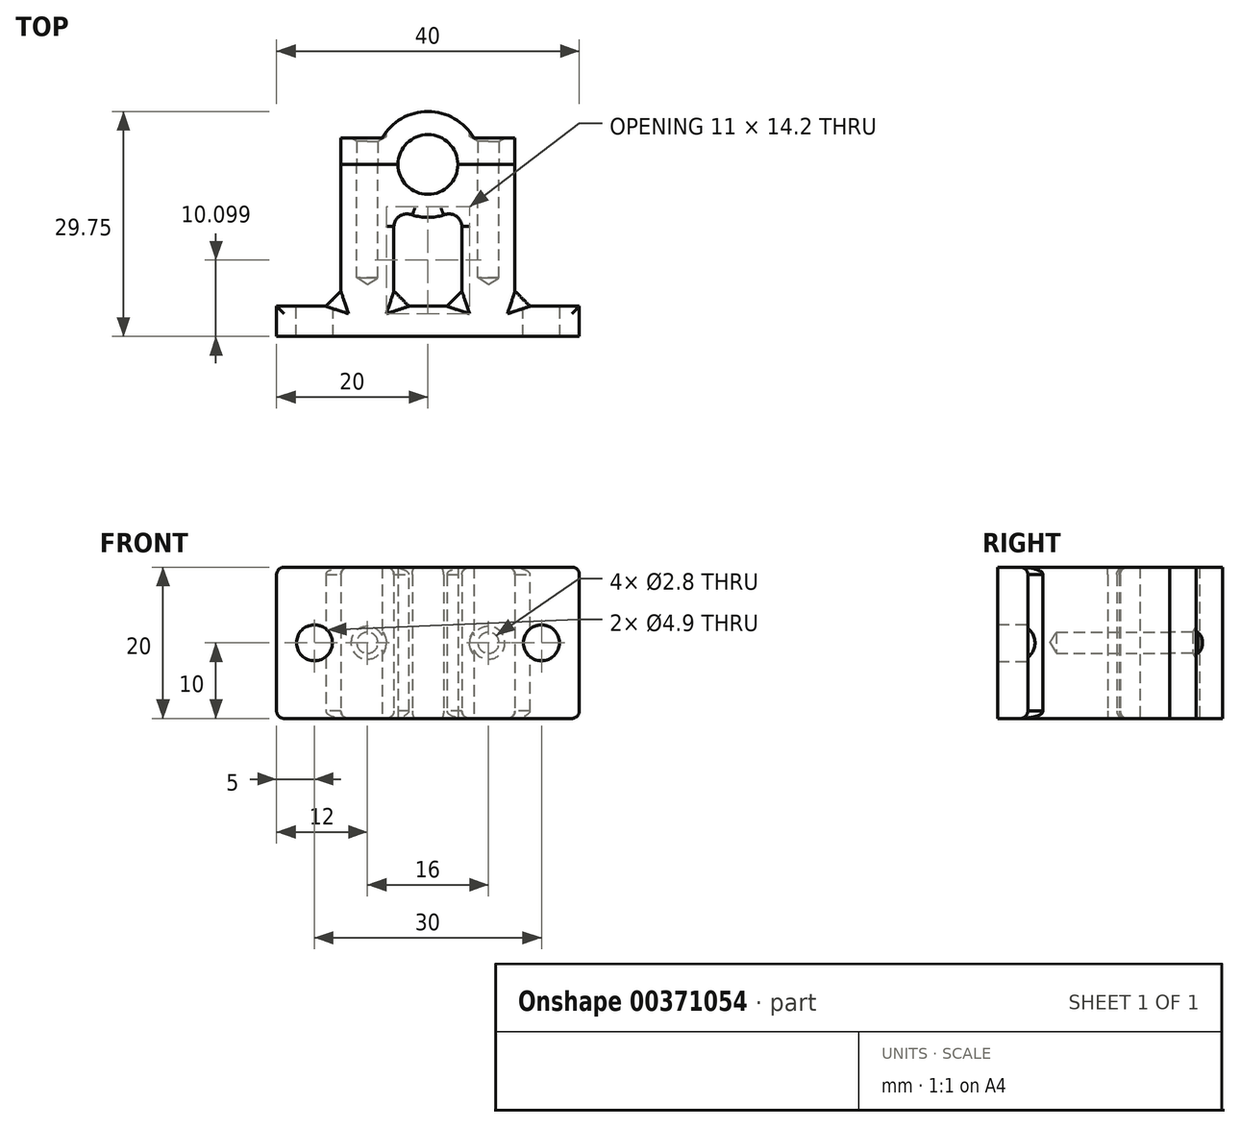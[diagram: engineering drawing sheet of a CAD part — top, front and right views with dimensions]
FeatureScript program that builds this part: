
annotation { "Feature Type Name" : "Feature", "Feature Type Description" : "" }
export const myFeature = defineFeature(function(context is Context, id is Id, definition is map)
    precondition{}
    {
        {
            var Q0;
            Q0=qCreatedBy(makeId("Top.planeOp"),FACE);
            var sketch = newSketch(context, id + "F0", { "sketchPlane" : qUnion([Q0])});
            skCircle(sketch, "E0", {"center": v(0, 0) * mm, "radius": 3.95 * mm, "construction": true});
            skLineSegment(sketch, "E1.bottom", {"start": v(-10, -22.75) * mm, "end": v(10, -22.75) * mm, "construction": true});
            skLineSegment(sketch, "E1.top", {"start": v(-10, 22.75) * mm, "end": v(10, 22.75) * mm, "construction": true});
            skLineSegment(sketch, "E1.left", {"start": v(-11.5, -22.75) * mm, "end": v(-11.5, 22.75) * mm, "construction": true});
            skLineSegment(sketch, "E1.right", {"start": v(11.5, -22.75) * mm, "end": v(11.5, 22.75) * mm, "construction": true});
            skLineSegment(sketch, "E2", {"start": v(0, 43.17) * mm, "end": v(0, -47.97) * mm, "construction": true});
            skPoint(sketch, "E2.startSnap0", {"position": v(0, -22.75) * mm});
            skLineSegment(sketch, "E3", {"start": v(-33.18, 0) * mm, "end": v(22.99, 0) * mm, "construction": true});
            skLineSegment(sketch, "E4", {"start": v(-3.95, 0) * mm, "end": v(-11.5, 0) * mm});
            skLineSegment(sketch, "E5", {"start": v(3.95, 0) * mm, "end": v(11.5, 0) * mm});
            skArc(sketch, "E6", {"start": v(-3.95, 0) * mm, "mid": v(0, 3.95) * mm, "end": v(3.95, 0) * mm});
            skArc(sketch, "E7", {"start": v(3.95, 0) * mm, "mid": v(0, -3.95) * mm, "end": v(-3.95, 0) * mm});
            skArc(sketch, "E8", {"start": v(7, 0) * mm, "mid": v(0, 7) * mm, "end": v(-7, 0) * mm, "construction": true});
            skLineSegment(sketch, "E9", {"start": v(-11.5, 0) * mm, "end": v(-11.5, 3.5) * mm});
            skLineSegment(sketch, "E10", {"start": v(-6.06, 3.5) * mm, "end": v(-11.5, 3.5) * mm});
            skLineSegment(sketch, "E11", {"start": v(6.06, 3.5) * mm, "end": v(11.5, 3.5) * mm});
            skLineSegment(sketch, "E12", {"start": v(11.5, 0) * mm, "end": v(11.5, 3.5) * mm});
            skArc(sketch, "E13", {"start": v(-6.06, 3.5) * mm, "mid": v(0, 7) * mm, "end": v(6.06, 3.5) * mm});
            skLineSegment(sketch, "E14.0", {"start": v(-9.14, -18.75) * mm, "end": v(10, -18.75) * mm, "construction": true});
            skLineSegment(sketch, "E15", {"start": v(-15, -18.75) * mm, "end": v(-9.14, -18.75) * mm});
            skLineSegment(sketch, "E16", {"start": v(-11.5, -18.75) * mm, "end": v(-11.5, 0) * mm});
            skLineSegment(sketch, "E17", {"start": v(15, -18.75) * mm, "end": v(10, -18.75) * mm});
            skLineSegment(sketch, "E18", {"start": v(11.5, -18.75) * mm, "end": v(11.5, 0) * mm});
            skArc(sketch, "E19", {"start": v(7, 0) * mm, "mid": v(0, -7) * mm, "end": v(-7, 0) * mm, "construction": true});
            skArc(sketch, "E20", {"start": v(-6, -3.6) * mm, "mid": v(0, -7) * mm, "end": v(6, -3.6) * mm});
            skPoint(sketch, "E21.endSnap0", {"position": v(-5.17, 3.5) * mm});
            skArc(sketch, "E22", {"start": v(-2.07, -6.69) * mm, "mid": v(-3.67, -6.8) * mm, "end": v(-4.5, -8.18) * mm});
            skArc(sketch, "E23.MirrorCS", {"start": v(2.07, -6.69) * mm, "mid": v(3.67, -6.8) * mm, "end": v(4.5, -8.18) * mm});
            skLineSegment(sketch, "E24", {"start": v(20, -22.75) * mm, "end": v(20, -18.75) * mm});
            skLineSegment(sketch, "E25", {"start": v(20, -18.75) * mm, "end": v(15, -18.75) * mm});
            skLineSegment(sketch, "E26.MirrorCS", {"start": v(-20, -18.75) * mm, "end": v(-15, -18.75) * mm});
            skLineSegment(sketch, "E27.MirrorCS", {"start": v(-20, -22.75) * mm, "end": v(-20, -18.75) * mm});
            skLineSegment(sketch, "E28.MirrorCS", {"start": v(-15, -26.7) * mm, "end": v(-15, 26.7) * mm, "construction": true});
            skLineSegment(sketch, "E29.MirrorCS", {"start": v(15, -26.7) * mm, "end": v(15, 26.7) * mm, "construction": true});
            skLineSegment(sketch, "E30", {"start": v(-20, -22.75) * mm, "end": v(20, -22.75) * mm});
            skLineSegment(sketch, "E31", {"start": v(4.5, -8.18) * mm, "end": v(4.5, -18.75) * mm});
            skLineSegment(sketch, "E32", {"start": v(4.5, -18.75) * mm, "end": v(-4.5, -18.75) * mm});
            skLineSegment(sketch, "E33.MirrorCS", {"start": v(-4.5, -8.18) * mm, "end": v(-4.5, -18.75) * mm});
            skSolve(sketch);
        }
        {
            var Q0;
            Q0=qCreatedBy(makeId("Front.planeOp"),FACE);
            var sketch = newSketch(context, id + "F1", { "sketchPlane" : qUnion([Q0])});
            skLineSegment(sketch, "E34", {"start": v(0, 0) * mm, "end": v(0, 20) * mm, "construction": true});
            skLineSegment(sketch, "E35", {"start": v(0, 20) * mm, "end": v(20, 20) * mm, "construction": true});
            skLineSegment(sketch, "E36", {"start": v(20, 20) * mm, "end": v(20, 0) * mm, "construction": true});
            skLineSegment(sketch, "E37", {"start": v(20, 0) * mm, "end": v(0, 0) * mm, "construction": true});
            skLineSegment(sketch, "E38.MirrorCS", {"start": v(0, 20) * mm, "end": v(-20, 20) * mm, "construction": true});
            skLineSegment(sketch, "E39.MirrorCS", {"start": v(-20, 0) * mm, "end": v(0, 0) * mm, "construction": true});
            skLineSegment(sketch, "E40.MirrorCS", {"start": v(-20, 20) * mm, "end": v(-20, 0) * mm, "construction": true});
            skLineSegment(sketch, "E41.MirrorCS", {"start": v(6, 20) * mm, "end": v(6, 0) * mm, "construction": true});
            skLineSegment(sketch, "E42.MirrorCS", {"start": v(10, 20) * mm, "end": v(10, 0) * mm, "construction": true});
            skLineSegment(sketch, "E43", {"start": v(-20, 20) * mm, "end": v(-10, 0) * mm, "construction": true});
            skLineSegment(sketch, "E44", {"start": v(-10, 20) * mm, "end": v(-20, 0) * mm, "construction": true});
            skLineSegment(sketch, "E45.MirrorCS", {"start": v(10, 20) * mm, "end": v(6, 0) * mm, "construction": true});
            skLineSegment(sketch, "E46.MirrorCS", {"start": v(6, 20) * mm, "end": v(10, 0) * mm, "construction": true});
            skLineSegment(sketch, "E47.MirrorCS", {"start": v(20, 20) * mm, "end": v(10, 0) * mm, "construction": true});
            skLineSegment(sketch, "E48.MirrorCS", {"start": v(10, 20) * mm, "end": v(20, 0) * mm, "construction": true});
            skLineSegment(sketch, "E49.MirrorCS", {"start": v(15, 10) * mm, "end": v(8, 10) * mm, "construction": true});
            skLineSegment(sketch, "E50.MirrorCS", {"start": v(-10, 20) * mm, "end": v(-10, 0) * mm, "construction": true});
            skLineSegment(sketch, "E51.MirrorCS", {"start": v(-10, 20) * mm, "end": v(-6, 0) * mm, "construction": true});
            skLineSegment(sketch, "E52.MirrorCS", {"start": v(-6, 20) * mm, "end": v(-10, 0) * mm, "construction": true});
            skLineSegment(sketch, "E53.MirrorCS", {"start": v(-6, 20) * mm, "end": v(-6, 0) * mm, "construction": true});
            skLineSegment(sketch, "E54.MirrorCS", {"start": v(-15, 10) * mm, "end": v(-8, 10) * mm, "construction": true});
            skSolve(sketch);
        }
        {
            var Q0;
            Q0=makeQuery(id+"F0.imprint","IMPRINT",FACE,{"disambiguationData":[TD([[makeQuery(id+"F0.imprint","IMPRINT",EDGE,{"derivedFrom":sQuery(id+"F0.wireOp",EDGE,"E4")}),1.0]])]});
            var Q1;
            {var subQ0=sQuery(id+"F0.wireOp",EDGE,"E20");var subQ1=sQuery(id+"F0.wireOp",EDGE,"fGXx5mKk-028a-ssRt-KOYL-Ndiq90U5VOPl");var subQ2=makeQuery(id+"F0.imprint","INTERSECT",VERTEX,{"derivedFrom":[subQ1,subQ0]});Q1=makeQuery(id+"F0.imprint","IMPRINT",FACE,{"disambiguationData":[TD([[makeQuery(id+"F0.imprint","IMPRINT",EDGE,{"disambiguationData":[TD([[subQ2,-1.0]])],"derivedFrom":subQ1}),1.0]])]});}
            var Q2;
            {var subQ0=sQuery(id+"F0.wireOp",EDGE,"E20");var subQ1=sQuery(id+"F0.wireOp",EDGE,"CvSH9Qos-IBVu-BQQu-liTP-uIPj88FDEuSd");var subQ2=makeQuery(id+"F0.imprint","INTERSECT",VERTEX,{"derivedFrom":[subQ1,subQ0]});Q2=makeQuery(id+"F0.imprint","IMPRINT",FACE,{"disambiguationData":[TD([[makeQuery(id+"F0.imprint","IMPRINT",EDGE,{"disambiguationData":[TD([[subQ2,1.0]])],"derivedFrom":subQ1}),1.0]])]});}
            var Q3;
            {var subQ0=sQuery(id+"F0.wireOp",EDGE,"E17");Q3=makeQuery(id+"F0.imprint","IMPRINT",FACE,{"disambiguationData":[TD([[makeQuery(id+"F0.imprint","IMPRINT",EDGE,{"derivedFrom":subQ0}),-1.0]])]});}
            var Q4;
            {var subQ3=sQuery(id+"F0.wireOp",EDGE,"ceada07a-6df1-444d-bf8f-508dd2f25667");Q4=makeQuery(id+"F0.imprint","IMPRINT",FACE,{"disambiguationData":[TD([[makeQuery(id+"F0.imprint","IMPRINT",EDGE,{"derivedFrom":subQ3}),-1.0]])]});}
            var Q5;
            {var subQ3=sQuery(id+"F0.wireOp",EDGE,"21435801-f3ad-4afe-81ca-bc311d5c01770.MirrorCS");Q5=makeQuery(id+"F0.imprint","IMPRINT",FACE,{"disambiguationData":[TD([[makeQuery(id+"F0.imprint","IMPRINT",EDGE,{"derivedFrom":subQ3}),1.0]])]});}
            var Q6;
            {var subQ0=sQuery(id+"F0.wireOp",EDGE,"E15");Q6=makeQuery(id+"F0.imprint","IMPRINT",FACE,{"disambiguationData":[TD([[makeQuery(id+"F0.imprint","IMPRINT",EDGE,{"derivedFrom":subQ0}),1.0]])]});}
            var Q7;
            {var subQ0=sQuery(id+"F0.wireOp",EDGE,"fiYNvXtu-JcpG-wVFz-9FR0-CaiYWWEELGmy");Q7=makeQuery(id+"F0.imprint","IMPRINT",FACE,{"disambiguationData":[TD([[makeQuery(id+"F0.imprint","IMPRINT",EDGE,{"derivedFrom":subQ0}),1.0]])]});}
            var Q8;
            {var subQ2=sQuery(id+"F0.wireOp",EDGE,"E26.MirrorCS");Q8=makeQuery(id+"F0.imprint","IMPRINT",FACE,{"disambiguationData":[TD([[makeQuery(id+"F0.imprint","IMPRINT",EDGE,{"derivedFrom":subQ2}),-1.0]])]});}
            extrude(context, id + "F2", {"entities" : qUnion([Q0, Q1, Q2, Q3, Q4, Q5, Q6, Q7, Q8]), "depth" : 20 * mm});
        }
        {
            var Q0;
            Q0=makeQuery(id+"F0.imprint","IMPRINT",FACE,{"disambiguationData":[TD([[makeQuery(id+"F0.imprint","IMPRINT",EDGE,{"derivedFrom":sQuery(id+"F0.wireOp",EDGE,"E4")}),-1.0]])]});
            var Q1;
            {var subQ0=sQuery(id+"F0.wireOp",EDGE,"E10");Q1=makeQuery(id+"F0.imprint","IMPRINT",FACE,{"disambiguationData":[TD([[makeQuery(id+"F0.imprint","IMPRINT",EDGE,{"derivedFrom":subQ0}),-1.0]])]});}
            var Q2;
            {var subQ0=sQuery(id+"F0.wireOp",EDGE,"E11");Q2=makeQuery(id+"F0.imprint","IMPRINT",FACE,{"disambiguationData":[TD([[makeQuery(id+"F0.imprint","IMPRINT",EDGE,{"derivedFrom":subQ0}),1.0]])]});}
            extrude(context, id + "F3", {"entities" : qUnion([Q0, Q1, Q2]), "depth" : 20 * mm});
        }
        {
            var Q0;
            Q0=sQuery(id+"F1.wireOp",VERTEX,"zXXnKSf7-GhJt-SI1w-yzcV-klMIAKRFoqqE.start");
            var Q1;
            Q1=sQuery(id+"F1.wireOp",VERTEX,"E49.MirrorCS.start");
            var Q2;
            Q2=makeQuery(id+"F2.opExtrude","SWEPT_BODY",BODY,{"disambiguationData":[OSD([sQuery(id+"F0.wireOp",EDGE,"E4"),sQuery(id+"F0.wireOp",EDGE,"E5"),sQuery(id+"F0.wireOp",EDGE,"E7"),sQuery(id+"F0.wireOp",EDGE,"Qp0b4A5F-PEZz-WxIl-w85g-mMOqEHtGHs0Y"),sQuery(id+"F0.wireOp",EDGE,"3GZM9fG6-5eXR-hhPL-hdbV-YrBfE3BmG3J5"),sQuery(id+"F0.wireOp",EDGE,"E16"),sQuery(id+"F0.wireOp",EDGE,"YOUf0rZS-7agO-fim9-izvp-ucZtZaTmQyXM"),sQuery(id+"F0.wireOp",EDGE,"E18"),sQuery(id+"F0.wireOp",EDGE,"fGXx5mKk-028a-ssRt-KOYL-Ndiq90U5VOPl"),sQuery(id+"F0.wireOp",EDGE,"KvWkPdP2-N5Ae-fyOq-ppFJ-d0FditwGePsY"),sQuery(id+"F0.wireOp",EDGE,"CvSH9Qos-IBVu-BQQu-liTP-uIPj88FDEuSd"),sQuery(id+"F0.wireOp",EDGE,"E20"),sQuery(id+"F0.wireOp",EDGE,"E22"),sQuery(id+"F0.wireOp",EDGE,"E23.MirrorCS"),sQuery(id+"F0.wireOp",EDGE,"lmKCdi61-SYqH-588H-mFMN-USzl79AIN7qr"),sQuery(id+"F0.wireOp",EDGE,"2fa183ca-1ded-41c0-80e5-ca687e3a55230.MirrorCS"),sQuery(id+"F0.wireOp",EDGE,"ceada07a-6df1-444d-bf8f-508dd2f25667"),sQuery(id+"F0.wireOp",EDGE,"21435801-f3ad-4afe-81ca-bc311d5c01770.MirrorCS")])]});
            hole(context, id + "F4", {"style" : HoleStyle.SIMPLE, "endStyle" : HoleEndStyle.BLIND, "oppositeDirection" : true, "holeDiameter" : 2.5 * mm, "holeDepth" : 30 * mm, "isTappedThrough" : true, "tappedDepth" : 12 * mm, "tapClearance" : 3, "locations" : qUnion([Q0, Q1]), "scope" : qUnion([Q2])});
        }
        {
            var Q0;
            Q0=sQuery(id+"F1.wireOp",VERTEX,"zXXnKSf7-GhJt-SI1w-yzcV-klMIAKRFoqqE.end");
            var Q1;
            Q1=sQuery(id+"F1.wireOp",VERTEX,"E49.MirrorCS.end");
            var Q2;
            Q2=sQuery(id+"F1.wireOp",VERTEX,"E54.MirrorCS.end");
            var Q3;
            Q3=makeQuery(id+"F3.opExtrude","SWEPT_BODY",BODY,{"disambiguationData":[OSD([sQuery(id+"F0.wireOp",EDGE,"E4"),sQuery(id+"F0.wireOp",EDGE,"E5"),sQuery(id+"F0.wireOp",EDGE,"E6"),sQuery(id+"F0.wireOp",EDGE,"E9"),sQuery(id+"F0.wireOp",EDGE,"E12"),sQuery(id+"F0.wireOp",EDGE,"E13"),sQuery(id+"F0.wireOp",EDGE,"E21"),sQuery(id+"F0.wireOp",EDGE,"c25b683a-cc0d-4ae4-92c7-48c638fb54a90.MirrorCS")])]});
            hole(context, id + "F5", {"style" : HoleStyle.SIMPLE, "endStyle" : HoleEndStyle.BLIND, "holeDiameter" : 2.8 * mm, "holeDepth" : 10 * mm, "isTappedThrough" : true, "tappedDepth" : 12 * mm, "tapClearance" : 3, "locations" : qUnion([Q0, Q1, Q2]), "scope" : qUnion([Q3])});
        }
        {
            var Q0;
            Q0=sQuery(id+"F1.wireOp",VERTEX,"zXXnKSf7-GhJt-SI1w-yzcV-klMIAKRFoqqE.end");
            var Q1;
            Q1=sQuery(id+"F1.wireOp",VERTEX,"E49.MirrorCS.end");
            var Q2;
            Q2=sQuery(id+"F1.wireOp",VERTEX,"E54.MirrorCS.end");
            var Q3;
            Q3=makeQuery(id+"F2.opExtrude","SWEPT_BODY",BODY,{"disambiguationData":[OSD([sQuery(id+"F0.wireOp",EDGE,"E4"),sQuery(id+"F0.wireOp",EDGE,"E5"),sQuery(id+"F0.wireOp",EDGE,"E7"),sQuery(id+"F0.wireOp",EDGE,"Qp0b4A5F-PEZz-WxIl-w85g-mMOqEHtGHs0Y"),sQuery(id+"F0.wireOp",EDGE,"3GZM9fG6-5eXR-hhPL-hdbV-YrBfE3BmG3J5"),sQuery(id+"F0.wireOp",EDGE,"E16"),sQuery(id+"F0.wireOp",EDGE,"YOUf0rZS-7agO-fim9-izvp-ucZtZaTmQyXM"),sQuery(id+"F0.wireOp",EDGE,"E18"),sQuery(id+"F0.wireOp",EDGE,"fGXx5mKk-028a-ssRt-KOYL-Ndiq90U5VOPl"),sQuery(id+"F0.wireOp",EDGE,"KvWkPdP2-N5Ae-fyOq-ppFJ-d0FditwGePsY"),sQuery(id+"F0.wireOp",EDGE,"CvSH9Qos-IBVu-BQQu-liTP-uIPj88FDEuSd"),sQuery(id+"F0.wireOp",EDGE,"E20"),sQuery(id+"F0.wireOp",EDGE,"E22"),sQuery(id+"F0.wireOp",EDGE,"E23.MirrorCS"),sQuery(id+"F0.wireOp",EDGE,"lmKCdi61-SYqH-588H-mFMN-USzl79AIN7qr"),sQuery(id+"F0.wireOp",EDGE,"2fa183ca-1ded-41c0-80e5-ca687e3a55230.MirrorCS"),sQuery(id+"F0.wireOp",EDGE,"ceada07a-6df1-444d-bf8f-508dd2f25667"),sQuery(id+"F0.wireOp",EDGE,"21435801-f3ad-4afe-81ca-bc311d5c01770.MirrorCS")])]});
            hole(context, id + "F6", {"style" : HoleStyle.SIMPLE, "endStyle" : HoleEndStyle.BLIND, "oppositeDirection" : true, "holeDiameter" : 2.8 * mm, "holeDepth" : 15 * mm, "isTappedThrough" : true, "tappedDepth" : 12 * mm, "tapClearance" : 3, "locations" : qUnion([Q0, Q1, Q2]), "scope" : qUnion([Q3])});
        }
        {
            var Q0;
            Q0=sQuery(id+"F1.wireOp",VERTEX,"zXXnKSf7-GhJt-SI1w-yzcV-klMIAKRFoqqE.start");
            var Q1;
            Q1=sQuery(id+"F1.wireOp",VERTEX,"E49.MirrorCS.start");
            var Q2;
            Q2=sQuery(id+"F1.wireOp",VERTEX,"E54.MirrorCS.start");
            var Q3;
            Q3=makeQuery(id+"F2.opExtrude","SWEPT_BODY",BODY,{"disambiguationData":[OSD([sQuery(id+"F0.wireOp",EDGE,"E4"),sQuery(id+"F0.wireOp",EDGE,"E5"),sQuery(id+"F0.wireOp",EDGE,"E7"),sQuery(id+"F0.wireOp",EDGE,"Qp0b4A5F-PEZz-WxIl-w85g-mMOqEHtGHs0Y"),sQuery(id+"F0.wireOp",EDGE,"3GZM9fG6-5eXR-hhPL-hdbV-YrBfE3BmG3J5"),sQuery(id+"F0.wireOp",EDGE,"E16"),sQuery(id+"F0.wireOp",EDGE,"YOUf0rZS-7agO-fim9-izvp-ucZtZaTmQyXM"),sQuery(id+"F0.wireOp",EDGE,"E18"),sQuery(id+"F0.wireOp",EDGE,"fGXx5mKk-028a-ssRt-KOYL-Ndiq90U5VOPl"),sQuery(id+"F0.wireOp",EDGE,"KvWkPdP2-N5Ae-fyOq-ppFJ-d0FditwGePsY"),sQuery(id+"F0.wireOp",EDGE,"CvSH9Qos-IBVu-BQQu-liTP-uIPj88FDEuSd"),sQuery(id+"F0.wireOp",EDGE,"E20"),sQuery(id+"F0.wireOp",EDGE,"E22"),sQuery(id+"F0.wireOp",EDGE,"E23.MirrorCS"),sQuery(id+"F0.wireOp",EDGE,"lmKCdi61-SYqH-588H-mFMN-USzl79AIN7qr"),sQuery(id+"F0.wireOp",EDGE,"2fa183ca-1ded-41c0-80e5-ca687e3a55230.MirrorCS"),sQuery(id+"F0.wireOp",EDGE,"ceada07a-6df1-444d-bf8f-508dd2f25667"),sQuery(id+"F0.wireOp",EDGE,"21435801-f3ad-4afe-81ca-bc311d5c01770.MirrorCS")])]});
            hole(context, id + "F7", {"style" : HoleStyle.SIMPLE, "endStyle" : HoleEndStyle.BLIND, "oppositeDirection" : true, "holeDiameter" : 4.9 * mm, "holeDepth" : 22.7 * mm, "isTappedThrough" : true, "tappedDepth" : 12 * mm, "tapClearance" : 3, "startFromSketch" : true, "locations" : qUnion([Q0, Q1, Q2]), "scope" : qUnion([Q3])});
        }
        {
            var Q0;
            Q0=qCreatedBy(makeId("Front.planeOp"),FACE);
            cPlane(context, id + "F8", {"entities" : qUnion([Q0]), "cplaneType" : CPlaneType.OFFSET, "offset" : 7 * mm, "oppositeDirection" : true, "width" : 150 * mm, "height" : 150 * mm});
        }
        {
            var Q0;
            Q0=qCreatedBy(id+"F8.planeOp",FACE);
            var sketch = newSketch(context, id + "F9", { "sketchPlane" : qUnion([Q0])});
            skLineSegment(sketch, "E55", {"start": v(0, 0) * mm, "end": v(0, 20) * mm, "construction": true});
            skLineSegment(sketch, "E56", {"start": v(0, 20) * mm, "end": v(15, 20) * mm, "construction": true});
            skLineSegment(sketch, "E57", {"start": v(15, 20) * mm, "end": v(15, 0) * mm, "construction": true});
            skLineSegment(sketch, "E58", {"start": v(15, 0) * mm, "end": v(0, 0) * mm, "construction": true});
            skLineSegment(sketch, "E59.MirrorCS", {"start": v(0, 20) * mm, "end": v(-15, 20) * mm, "construction": true});
            skLineSegment(sketch, "E60.MirrorCS", {"start": v(-15, 0) * mm, "end": v(0, 0) * mm, "construction": true});
            skLineSegment(sketch, "E61.MirrorCS", {"start": v(-15, 20) * mm, "end": v(-15, 0) * mm, "construction": true});
            skLineSegment(sketch, "E62.0", {"start": v(-10, 20) * mm, "end": v(-10, 0) * mm, "construction": true});
            skLineSegment(sketch, "E63.0", {"start": v(-6, 20) * mm, "end": v(-6, 0) * mm, "construction": true});
            skLineSegment(sketch, "E64.MirrorCS", {"start": v(6, 20) * mm, "end": v(6, 0) * mm, "construction": true});
            skLineSegment(sketch, "E65.MirrorCS", {"start": v(10, 20) * mm, "end": v(10, 0) * mm, "construction": true});
            skLineSegment(sketch, "E66", {"start": v(-15, 20) * mm, "end": v(-10, 0) * mm, "construction": true});
            skLineSegment(sketch, "E67", {"start": v(-10, 10) * mm, "end": v(-15, 0) * mm, "construction": true});
            skLineSegment(sketch, "E68", {"start": v(-10, 20) * mm, "end": v(-6, 0) * mm, "construction": true});
            skLineSegment(sketch, "E69", {"start": v(-6, 20) * mm, "end": v(-10, 0) * mm, "construction": true});
            skLineSegment(sketch, "E70.MirrorCS", {"start": v(10, 20) * mm, "end": v(6, 0) * mm, "construction": true});
            skLineSegment(sketch, "E71.MirrorCS", {"start": v(6, 20) * mm, "end": v(10, 0) * mm, "construction": true});
            skLineSegment(sketch, "E72.MirrorCS", {"start": v(15, 20) * mm, "end": v(10, 0) * mm, "construction": true});
            skLineSegment(sketch, "E73.MirrorCS", {"start": v(10, 10) * mm, "end": v(15, 0) * mm, "construction": true});
            skLineSegment(sketch, "E74", {"start": v(-12.5, 10) * mm, "end": v(-8, 10) * mm, "construction": true});
            skLineSegment(sketch, "E75.MirrorCS", {"start": v(12.5, 10) * mm, "end": v(8, 10) * mm, "construction": true});
            skSolve(sketch);
        }
        {
            var Q0;
            Q0=sQuery(id+"F9.wireOp",VERTEX,"E75.MirrorCS.end");
            var Q1;
            Q1=sQuery(id+"F9.wireOp",VERTEX,"E74.end");
            var Q2;
            Q2=makeQuery(id+"F3.opExtrude","SWEPT_BODY",BODY,{"disambiguationData":[OSD([sQuery(id+"F0.wireOp",EDGE,"E4"),sQuery(id+"F0.wireOp",EDGE,"E5"),sQuery(id+"F0.wireOp",EDGE,"E6"),sQuery(id+"F0.wireOp",EDGE,"E9"),sQuery(id+"F0.wireOp",EDGE,"E12"),sQuery(id+"F0.wireOp",EDGE,"E13"),sQuery(id+"F0.wireOp",EDGE,"E21"),sQuery(id+"F0.wireOp",EDGE,"c25b683a-cc0d-4ae4-92c7-48c638fb54a90.MirrorCS")])]});
            hole(context, id + "F10", {"style" : HoleStyle.SIMPLE, "endStyle" : HoleEndStyle.BLIND, "oppositeDirection" : true, "holeDiameter" : 5 * mm, "holeDepth" : 3.3 * mm, "isTappedThrough" : true, "tappedDepth" : 12 * mm, "tapClearance" : 3, "startFromSketch" : true, "locations" : qUnion([Q0, Q1]), "scope" : qUnion([Q2])});
        }
        {
            var Q0;
            Q0=makeQuery(id+"F3.opExtrude","CAP_EDGE",EDGE,{"disambiguationData":[OSD([sQuery(id+"F0.wireOp",EDGE,"E12")])],"isStart":true});
            var Q1;
            Q1=makeQuery(id+"F2.opExtrude","CAP_EDGE",EDGE,{"disambiguationData":[OSD([sQuery(id+"F0.wireOp",EDGE,"E18")])],"isStart":true});
            var Q2;
            Q2=makeQuery(id+"F2.opExtrude","CAP_EDGE",EDGE,{"disambiguationData":[OSD([sQuery(id+"F0.wireOp",EDGE,"2fa183ca-1ded-41c0-80e5-ca687e3a55230.MirrorCS")])],"isStart":true});
            var Q3;
            Q3=makeQuery(id+"F2.opExtrude","CAP_EDGE",EDGE,{"disambiguationData":[OSD([sQuery(id+"F0.wireOp",EDGE,"lmKCdi61-SYqH-588H-mFMN-USzl79AIN7qr")])],"isStart":true});
            var Q4;
            Q4=makeQuery(id+"F2.opExtrude","CAP_EDGE",EDGE,{"disambiguationData":[OSD([sQuery(id+"F0.wireOp",EDGE,"E16")])],"isStart":true});
            var Q5;
            Q5=makeQuery(id+"F3.opExtrude","CAP_EDGE",EDGE,{"disambiguationData":[OSD([sQuery(id+"F0.wireOp",EDGE,"E9")])],"isStart":true});
            var Q6;
            Q6=makeQuery(id+"F2.opExtrude","CAP_EDGE",EDGE,{"disambiguationData":[OSD([sQuery(id+"F0.wireOp",EDGE,"lmKCdi61-SYqH-588H-mFMN-USzl79AIN7qr")])],"isStart":false});
            var Q7;
            Q7=makeQuery(id+"F2.opExtrude","CAP_EDGE",EDGE,{"disambiguationData":[OSD([sQuery(id+"F0.wireOp",EDGE,"E16")])],"isStart":false});
            var Q8;
            Q8=makeQuery(id+"F3.opExtrude","CAP_EDGE",EDGE,{"disambiguationData":[OSD([sQuery(id+"F0.wireOp",EDGE,"E9")])],"isStart":false});
            var Q9;
            Q9=makeQuery(id+"F2.opExtrude","CAP_EDGE",EDGE,{"disambiguationData":[OSD([sQuery(id+"F0.wireOp",EDGE,"2fa183ca-1ded-41c0-80e5-ca687e3a55230.MirrorCS")])],"isStart":false});
            var Q10;
            Q10=makeQuery(id+"F2.opExtrude","CAP_EDGE",EDGE,{"disambiguationData":[OSD([sQuery(id+"F0.wireOp",EDGE,"E18")])],"isStart":false});
            var Q11;
            Q11=makeQuery(id+"F3.opExtrude","CAP_EDGE",EDGE,{"disambiguationData":[OSD([sQuery(id+"F0.wireOp",EDGE,"E12")])],"isStart":false});
            var Q12;
            Q12=makeQuery(id+"F2.opExtrude","CAP_EDGE",EDGE,{"disambiguationData":[OSD([sQuery(id+"F0.wireOp",EDGE,"ceada07a-6df1-444d-bf8f-508dd2f25667")])],"isStart":false});
            var Q13;
            Q13=makeQuery(id+"F2.opExtrude","CAP_EDGE",EDGE,{"disambiguationData":[OSD([sQuery(id+"F0.wireOp",EDGE,"21435801-f3ad-4afe-81ca-bc311d5c01770.MirrorCS")])],"isStart":false});
            var Q14;
            Q14=makeQuery(id+"F2.opExtrude","CAP_EDGE",EDGE,{"disambiguationData":[OSD([sQuery(id+"F0.wireOp",EDGE,"fGXx5mKk-028a-ssRt-KOYL-Ndiq90U5VOPl")])],"isStart":false});
            var Q15;
            Q15=makeQuery(id+"F2.opExtrude","CAP_EDGE",EDGE,{"disambiguationData":[OSD([sQuery(id+"F0.wireOp",EDGE,"E22")])],"isStart":false});
            var Q16;
            Q16=makeQuery(id+"F2.opExtrude","CAP_EDGE",EDGE,{"disambiguationData":[OSD([sQuery(id+"F0.wireOp",EDGE,"E20")])],"isStart":false});
            var Q17;
            Q17=makeQuery(id+"F2.opExtrude","CAP_EDGE",EDGE,{"disambiguationData":[OSD([sQuery(id+"F0.wireOp",EDGE,"E23.MirrorCS")])],"isStart":false});
            var Q18;
            Q18=makeQuery(id+"F2.opExtrude","CAP_EDGE",EDGE,{"disambiguationData":[OSD([sQuery(id+"F0.wireOp",EDGE,"CvSH9Qos-IBVu-BQQu-liTP-uIPj88FDEuSd")])],"isStart":false});
            var Q19;
            Q19=makeQuery(id+"F2.opExtrude","CAP_EDGE",EDGE,{"disambiguationData":[OSD([sQuery(id+"F0.wireOp",EDGE,"KvWkPdP2-N5Ae-fyOq-ppFJ-d0FditwGePsY")])],"isStart":false});
            var Q20;
            Q20=makeQuery(id+"F2.opExtrude","CAP_EDGE",EDGE,{"disambiguationData":[OSD([sQuery(id+"F0.wireOp",EDGE,"E22")])],"isStart":true});
            var Q21;
            Q21=makeQuery(id+"F2.opExtrude","CAP_EDGE",EDGE,{"disambiguationData":[OSD([sQuery(id+"F0.wireOp",EDGE,"E20")])],"isStart":true});
            var Q22;
            Q22=makeQuery(id+"F2.opExtrude","CAP_EDGE",EDGE,{"disambiguationData":[OSD([sQuery(id+"F0.wireOp",EDGE,"E23.MirrorCS")])],"isStart":true});
            var Q23;
            Q23=makeQuery(id+"F2.opExtrude","CAP_EDGE",EDGE,{"disambiguationData":[OSD([sQuery(id+"F0.wireOp",EDGE,"CvSH9Qos-IBVu-BQQu-liTP-uIPj88FDEuSd")])],"isStart":true});
            var Q24;
            Q24=makeQuery(id+"F2.opExtrude","CAP_EDGE",EDGE,{"disambiguationData":[OSD([sQuery(id+"F0.wireOp",EDGE,"ceada07a-6df1-444d-bf8f-508dd2f25667")])],"isStart":true});
            var Q25;
            Q25=makeQuery(id+"F2.opExtrude","CAP_EDGE",EDGE,{"disambiguationData":[OSD([sQuery(id+"F0.wireOp",EDGE,"KvWkPdP2-N5Ae-fyOq-ppFJ-d0FditwGePsY")])],"isStart":true});
            var Q26;
            Q26=makeQuery(id+"F2.opExtrude","CAP_EDGE",EDGE,{"disambiguationData":[OSD([sQuery(id+"F0.wireOp",EDGE,"21435801-f3ad-4afe-81ca-bc311d5c01770.MirrorCS")])],"isStart":true});
            var Q27;
            Q27=makeQuery(id+"F2.opExtrude","CAP_EDGE",EDGE,{"disambiguationData":[OSD([sQuery(id+"F0.wireOp",EDGE,"fGXx5mKk-028a-ssRt-KOYL-Ndiq90U5VOPl")])],"isStart":true});
            var Q28;
            Q28=makeQuery(id+"F2.opExtrude","CAP_EDGE",EDGE,{"disambiguationData":[OSD([sQuery(id+"F0.wireOp",EDGE,"3GZM9fG6-5eXR-hhPL-hdbV-YrBfE3BmG3J5")])],"isStart":true});
            var Q29;
            Q29=makeQuery(id+"F2.opExtrude","CAP_EDGE",EDGE,{"disambiguationData":[OSD([sQuery(id+"F0.wireOp",EDGE,"3GZM9fG6-5eXR-hhPL-hdbV-YrBfE3BmG3J5")])],"isStart":false});
            var Q30;
            Q30=makeQuery(id+"F2.opExtrude","CAP_EDGE",EDGE,{"disambiguationData":[OSD([sQuery(id+"F0.wireOp",EDGE,"YOUf0rZS-7agO-fim9-izvp-ucZtZaTmQyXM")])],"isStart":false});
            var Q31;
            Q31=makeQuery(id+"F2.opExtrude","CAP_EDGE",EDGE,{"disambiguationData":[OSD([sQuery(id+"F0.wireOp",EDGE,"YOUf0rZS-7agO-fim9-izvp-ucZtZaTmQyXM")])],"isStart":true});
            var Q32;
            Q32=makeQuery(id+"F2.opExtrude","CAP_EDGE",EDGE,{"disambiguationData":[OSD([sQuery(id+"F0.wireOp",EDGE,"E26.MirrorCS")])],"isStart":false});
            var Q33;
            Q33=makeQuery(id+"F2.opExtrude","CAP_EDGE",EDGE,{"disambiguationData":[OSD([sQuery(id+"F0.wireOp",EDGE,"E27.MirrorCS")])],"isStart":false});
            var Q34;
            Q34=makeQuery(id+"F2.opExtrude","CAP_EDGE",EDGE,{"disambiguationData":[OSD([sQuery(id+"F0.wireOp",EDGE,"E24")])],"isStart":false});
            var Q35;
            Q35=makeQuery(id+"F2.opExtrude","CAP_EDGE",EDGE,{"disambiguationData":[OSD([sQuery(id+"F0.wireOp",EDGE,"E25")])],"isStart":false});
            var Q36;
            Q36=makeQuery(id+"F2.opExtrude","CAP_EDGE",EDGE,{"disambiguationData":[OSD([sQuery(id+"F0.wireOp",EDGE,"E26.MirrorCS")])],"isStart":true});
            var Q37;
            Q37=makeQuery(id+"F2.opExtrude","CAP_EDGE",EDGE,{"disambiguationData":[OSD([sQuery(id+"F0.wireOp",EDGE,"E27.MirrorCS")])],"isStart":true});
            var Q38;
            Q38=makeQuery(id+"F2.opExtrude","CAP_EDGE",EDGE,{"disambiguationData":[OSD([sQuery(id+"F0.wireOp",EDGE,"E25")])],"isStart":true});
            var Q39;
            Q39=makeQuery(id+"F2.opExtrude","CAP_EDGE",EDGE,{"disambiguationData":[OSD([sQuery(id+"F0.wireOp",EDGE,"E24")])],"isStart":true});
            var Q40;
            Q40=makeQuery(id+"F2.opExtrude","CAP_EDGE",EDGE,{"disambiguationData":[OSD([sQuery(id+"F0.wireOp",EDGE,"E33.MirrorCS")])],"isStart":false});
            var Q41;
            Q41=makeQuery(id+"F2.opExtrude","CAP_EDGE",EDGE,{"disambiguationData":[OSD([sQuery(id+"F0.wireOp",EDGE,"E31")])],"isStart":false});
            var Q42;
            Q42=makeQuery(id+"F2.opExtrude","CAP_EDGE",EDGE,{"disambiguationData":[OSD([sQuery(id+"F0.wireOp",EDGE,"E33.MirrorCS")])],"isStart":true});
            var Q43;
            Q43=makeQuery(id+"F2.opExtrude","CAP_EDGE",EDGE,{"disambiguationData":[OSD([sQuery(id+"F0.wireOp",EDGE,"E31")])],"isStart":true});
            var Q44;
            Q44=makeQuery(id+"F2.opExtrude","CAP_EDGE",EDGE,{"disambiguationData":[OSD([sQuery(id+"F0.wireOp",EDGE,"E32")])],"isStart":true});
            var Q45;
            Q45=makeQuery(id+"F2.opExtrude","CAP_EDGE",EDGE,{"disambiguationData":[OSD([sQuery(id+"F0.wireOp",EDGE,"E32")])],"isStart":false});
            fillet(context, id + "F11", {"entities" : qUnion([Q0, Q1, Q2, Q3, Q4, Q5, Q6, Q7, Q8, Q9, Q10, Q11, Q12, Q13, Q14, Q15, Q16, Q17, Q18, Q19, Q20, Q21, Q22, Q23, Q24, Q25, Q26, Q27, Q28, Q29, Q30, Q31, Q32, Q33, Q34, Q35, Q36, Q37, Q38, Q39, Q40, Q41, Q42, Q43, Q44, Q45]), "radius" : 1 * mm, "tangentPropagation" : true, "allowEdgeOverflow" : false});
        }
        {
            var Q0;
            Q0=makeQuery(id+"F2.opExtrude","SWEPT_EDGE",EDGE,{"disambiguationData":[OSD([sQuery(id+"F0.wireOp",EDGE,"E31"),sQuery(id+"F0.wireOp",EDGE,"E32")])]});
            var Q1;
            Q1=makeQuery(id+"F2.opExtrude","SWEPT_EDGE",EDGE,{"disambiguationData":[OSD([sQuery(id+"F0.wireOp",EDGE,"E32"),sQuery(id+"F0.wireOp",EDGE,"E33.MirrorCS")])]});
            var Q2;
            Q2=makeQuery(id+"F2.opExtrude","SWEPT_EDGE",EDGE,{"disambiguationData":[OSD([sQuery(id+"F0.wireOp",EDGE,"E17"),sQuery(id+"F0.wireOp",EDGE,"E18")])]});
            var Q3;
            Q3=makeQuery(id+"F2.opExtrude","SWEPT_EDGE",EDGE,{"disambiguationData":[OSD([sQuery(id+"F0.wireOp",EDGE,"E15"),sQuery(id+"F0.wireOp",EDGE,"E16")])]});
            chamfer(context, id + "F12", {"entities" : qUnion([Q0, Q1, Q2, Q3]), "width" : 2 * mm, "tangentPropagation" : true});
        }
    });
